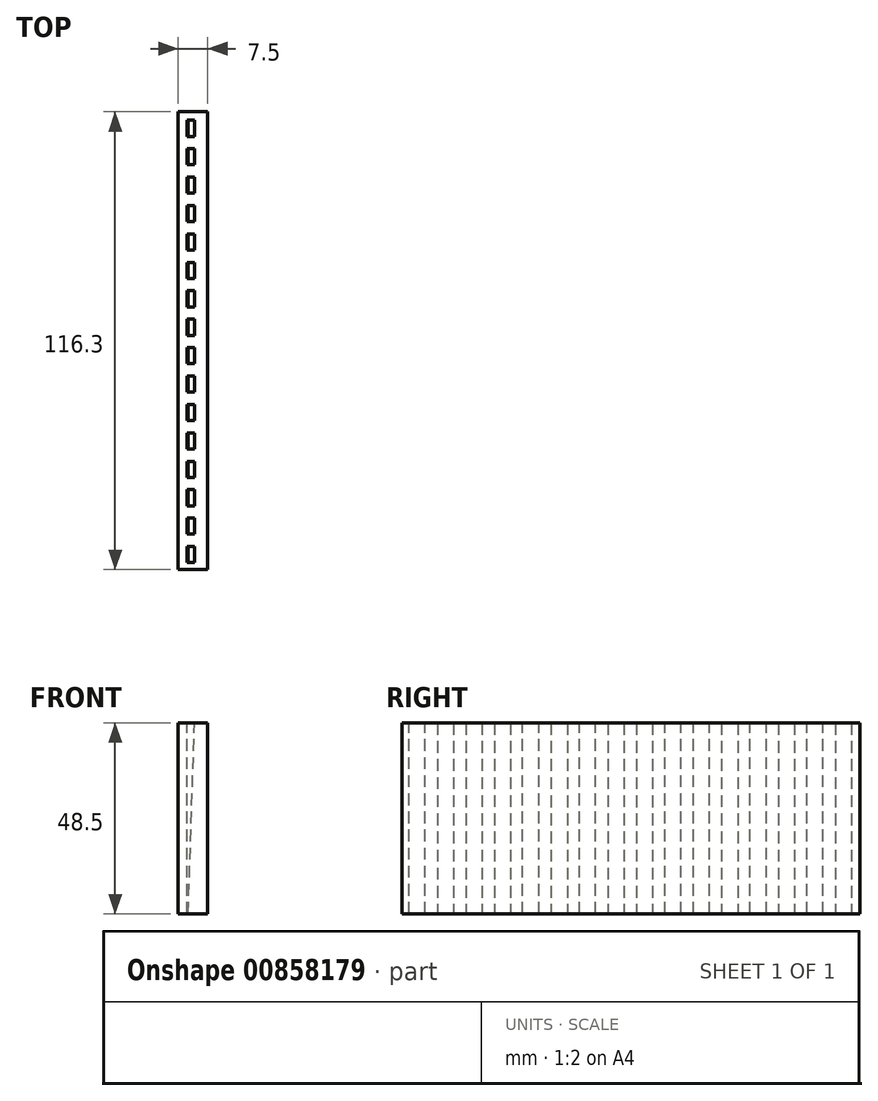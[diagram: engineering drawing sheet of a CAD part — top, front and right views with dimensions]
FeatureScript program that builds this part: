
annotation { "Feature Type Name" : "Feature", "Feature Type Description" : "" }
export const myFeature = defineFeature(function(context is Context, id is Id, definition is map)
    precondition{}
    {
        {
            var Q0;
            Q0=qCreatedBy(makeId("Right.planeOp"),FACE);
            var sketch = newSketch(context, id + "F0", { "sketchPlane" : qUnion([Q0])});
            skLineSegment(sketch, "E0.bottom", {"start": v(-70.88, 2.95) * mm, "end": v(80.42, 2.95) * mm});
            skLineSegment(sketch, "E0.top", {"start": v(-70.88, -45.55) * mm, "end": v(80.42, -45.55) * mm});
            skLineSegment(sketch, "E0.left", {"start": v(-70.88, 2.95) * mm, "end": v(-70.88, -45.55) * mm});
            skLineSegment(sketch, "E0.right", {"start": v(80.42, 2.95) * mm, "end": v(80.42, -45.55) * mm});
            skSolve(sketch);
        }
        {
            var Q0;
            Q0=makeQuery(id+"F0.imprint","IMPRINT",FACE,{"disambiguationData":[TD([[makeQuery(id+"F0.imprint","IMPRINT",EDGE,{"derivedFrom":sQuery(id+"F0.wireOp",EDGE,"E0.bottom")}),-1.0]])]});
            extrude(context, id + "F1", {"entities" : qUnion([Q0]), "depth" : 8 * mm, "offsetDistance" : 25 * mm});
        }
        {
            var Q0;
            Q0=makeQuery(id+"F1.opExtrude","SWEPT_FACE",FACE,{"disambiguationData":[OSD([sQuery(id+"F0.wireOp",EDGE,"E0.bottom")])]});
            var sketch = newSketch(context, id + "F2", { "sketchPlane" : qUnion([Q0])});
            skLineSegment(sketch, "E1.bottom", {"start": v(0.8, -69.15) * mm, "end": v(2.64, -69.15) * mm});
            skLineSegment(sketch, "E1.top", {"start": v(0.8, -65.05) * mm, "end": v(2.64, -65.05) * mm});
            skLineSegment(sketch, "E1.left", {"start": v(0.8, -69.15) * mm, "end": v(0.8, -65.05) * mm});
            skLineSegment(sketch, "E1.right", {"start": v(2.64, -69.15) * mm, "end": v(2.64, -65.05) * mm});
            skLineSegment(sketch, "E2.0.1.0", {"start": v(0.8, -61.93) * mm, "end": v(0.8, -57.83) * mm});
            skLineSegment(sketch, "E2.0.1.1", {"start": v(2.64, -61.93) * mm, "end": v(2.64, -57.83) * mm});
            skLineSegment(sketch, "E2.0.1.2", {"start": v(0.8, -61.93) * mm, "end": v(2.64, -61.93) * mm});
            skLineSegment(sketch, "E2.0.1.3", {"start": v(0.8, -57.83) * mm, "end": v(2.64, -57.83) * mm});
            skLineSegment(sketch, "E2.0.2.0", {"start": v(0.8, -54.7) * mm, "end": v(0.8, -50.6) * mm});
            skLineSegment(sketch, "E2.0.2.1", {"start": v(2.64, -54.7) * mm, "end": v(2.64, -50.6) * mm});
            skLineSegment(sketch, "E2.0.2.2", {"start": v(0.8, -54.7) * mm, "end": v(2.64, -54.7) * mm});
            skLineSegment(sketch, "E2.0.2.3", {"start": v(0.8, -50.6) * mm, "end": v(2.64, -50.6) * mm});
            skLineSegment(sketch, "E2.0.3.0", {"start": v(0.8, -47.49) * mm, "end": v(0.8, -43.39) * mm});
            skLineSegment(sketch, "E2.0.3.1", {"start": v(2.64, -47.49) * mm, "end": v(2.64, -43.39) * mm});
            skLineSegment(sketch, "E2.0.3.2", {"start": v(0.8, -47.49) * mm, "end": v(2.64, -47.49) * mm});
            skLineSegment(sketch, "E2.0.3.3", {"start": v(0.8, -43.39) * mm, "end": v(2.64, -43.39) * mm});
            skLineSegment(sketch, "E2.0.4.0", {"start": v(0.8, -40.27) * mm, "end": v(0.8, -36.17) * mm});
            skLineSegment(sketch, "E2.0.4.1", {"start": v(2.64, -40.27) * mm, "end": v(2.64, -36.17) * mm});
            skLineSegment(sketch, "E2.0.4.2", {"start": v(0.8, -40.27) * mm, "end": v(2.64, -40.27) * mm});
            skLineSegment(sketch, "E2.0.4.3", {"start": v(0.8, -36.17) * mm, "end": v(2.64, -36.17) * mm});
            skLineSegment(sketch, "E2.0.5.0", {"start": v(0.8, -33.05) * mm, "end": v(0.8, -28.95) * mm});
            skLineSegment(sketch, "E2.0.5.1", {"start": v(2.64, -33.05) * mm, "end": v(2.64, -28.95) * mm});
            skLineSegment(sketch, "E2.0.5.2", {"start": v(0.8, -33.05) * mm, "end": v(2.64, -33.05) * mm});
            skLineSegment(sketch, "E2.0.5.3", {"start": v(0.8, -28.95) * mm, "end": v(2.64, -28.95) * mm});
            skLineSegment(sketch, "E2.0.6.0", {"start": v(0.8, -25.83) * mm, "end": v(0.8, -21.73) * mm});
            skLineSegment(sketch, "E2.0.6.1", {"start": v(2.64, -25.83) * mm, "end": v(2.64, -21.73) * mm});
            skLineSegment(sketch, "E2.0.6.2", {"start": v(0.8, -25.83) * mm, "end": v(2.64, -25.83) * mm});
            skLineSegment(sketch, "E2.0.6.3", {"start": v(0.8, -21.73) * mm, "end": v(2.64, -21.73) * mm});
            skLineSegment(sketch, "E2.0.7.0", {"start": v(0.8, -18.6) * mm, "end": v(0.8, -14.5) * mm});
            skLineSegment(sketch, "E2.0.7.1", {"start": v(2.64, -18.6) * mm, "end": v(2.64, -14.5) * mm});
            skLineSegment(sketch, "E2.0.7.2", {"start": v(0.8, -18.6) * mm, "end": v(2.64, -18.6) * mm});
            skLineSegment(sketch, "E2.0.7.3", {"start": v(0.8, -14.5) * mm, "end": v(2.64, -14.5) * mm});
            skLineSegment(sketch, "E2.0.8.0", {"start": v(0.8, -11.39) * mm, "end": v(0.8, -7.29) * mm});
            skLineSegment(sketch, "E2.0.8.1", {"start": v(2.64, -11.39) * mm, "end": v(2.64, -7.29) * mm});
            skLineSegment(sketch, "E2.0.8.2", {"start": v(0.8, -11.39) * mm, "end": v(2.64, -11.39) * mm});
            skLineSegment(sketch, "E2.0.8.3", {"start": v(0.8, -7.29) * mm, "end": v(2.64, -7.29) * mm});
            skLineSegment(sketch, "E2.0.9.0", {"start": v(0.8, -4.17) * mm, "end": v(0.8, -0.07) * mm});
            skLineSegment(sketch, "E2.0.9.1", {"start": v(2.64, -4.17) * mm, "end": v(2.64, -0.07) * mm});
            skLineSegment(sketch, "E2.0.9.2", {"start": v(0.8, -4.17) * mm, "end": v(2.64, -4.17) * mm});
            skLineSegment(sketch, "E2.0.9.3", {"start": v(0.8, -0.07) * mm, "end": v(2.64, -0.07) * mm});
            skLineSegment(sketch, "E2.0.10.0", {"start": v(0.8, 3.05) * mm, "end": v(0.8, 7.15) * mm});
            skLineSegment(sketch, "E2.0.10.1", {"start": v(2.64, 3.05) * mm, "end": v(2.64, 7.15) * mm});
            skLineSegment(sketch, "E2.0.10.2", {"start": v(0.8, 3.05) * mm, "end": v(2.64, 3.05) * mm});
            skLineSegment(sketch, "E2.0.10.3", {"start": v(0.8, 7.15) * mm, "end": v(2.64, 7.15) * mm});
            skLineSegment(sketch, "E2.0.11.0", {"start": v(0.8, 10.27) * mm, "end": v(0.8, 14.37) * mm});
            skLineSegment(sketch, "E2.0.11.1", {"start": v(2.64, 10.27) * mm, "end": v(2.64, 14.37) * mm});
            skLineSegment(sketch, "E2.0.11.2", {"start": v(0.8, 10.27) * mm, "end": v(2.64, 10.27) * mm});
            skLineSegment(sketch, "E2.0.11.3", {"start": v(0.8, 14.37) * mm, "end": v(2.64, 14.37) * mm});
            skLineSegment(sketch, "E2.0.12.0", {"start": v(0.8, 17.5) * mm, "end": v(0.8, 21.6) * mm});
            skLineSegment(sketch, "E2.0.12.1", {"start": v(2.64, 17.5) * mm, "end": v(2.64, 21.6) * mm});
            skLineSegment(sketch, "E2.0.12.2", {"start": v(0.8, 17.5) * mm, "end": v(2.64, 17.5) * mm});
            skLineSegment(sketch, "E2.0.12.3", {"start": v(0.8, 21.6) * mm, "end": v(2.64, 21.6) * mm});
            skLineSegment(sketch, "E2.0.13.0", {"start": v(0.8, 24.71) * mm, "end": v(0.8, 28.81) * mm});
            skLineSegment(sketch, "E2.0.13.1", {"start": v(2.64, 24.71) * mm, "end": v(2.64, 28.81) * mm});
            skLineSegment(sketch, "E2.0.13.2", {"start": v(0.8, 24.71) * mm, "end": v(2.64, 24.71) * mm});
            skLineSegment(sketch, "E2.0.13.3", {"start": v(0.8, 28.81) * mm, "end": v(2.64, 28.81) * mm});
            skLineSegment(sketch, "E2.0.14.0", {"start": v(0.8, 31.93) * mm, "end": v(0.8, 36.03) * mm});
            skLineSegment(sketch, "E2.0.14.1", {"start": v(2.64, 31.93) * mm, "end": v(2.64, 36.03) * mm});
            skLineSegment(sketch, "E2.0.14.2", {"start": v(0.8, 31.93) * mm, "end": v(2.64, 31.93) * mm});
            skLineSegment(sketch, "E2.0.14.3", {"start": v(0.8, 36.03) * mm, "end": v(2.64, 36.03) * mm});
            skLineSegment(sketch, "E2.0.15.0", {"start": v(0.8, 39.15) * mm, "end": v(0.8, 43.25) * mm});
            skLineSegment(sketch, "E2.0.15.1", {"start": v(2.64, 39.15) * mm, "end": v(2.64, 43.25) * mm});
            skLineSegment(sketch, "E2.0.15.2", {"start": v(0.8, 39.15) * mm, "end": v(2.64, 39.15) * mm});
            skLineSegment(sketch, "E2.0.15.3", {"start": v(0.8, 43.25) * mm, "end": v(2.64, 43.25) * mm});
            skLineSegment(sketch, "E2.direction1", {"start": v(0.8, -69.15) * mm, "end": v(0.8, -69.15) * mm});
            skLineSegment(sketch, "E2.direction2", {"start": v(0.8, -69.15) * mm, "end": v(0.8, -61.93) * mm, "construction": true});
            skSolve(sketch);
        }
        {
            var Q0;
            Q0=makeQuery(id+"F1.opExtrude","SWEPT_FACE",FACE,{"disambiguationData":[OSD([sQuery(id+"F0.wireOp",EDGE,"E0.top")])]});
            var sketch = newSketch(context, id + "F3", { "sketchPlane" : qUnion([Q0])});
            skLineSegment(sketch, "E3.bottom", {"start": v(0.78, 69.14) * mm, "end": v(1.03, 69.14) * mm});
            skLineSegment(sketch, "E3.top", {"start": v(0.78, 65.04) * mm, "end": v(1.03, 65.04) * mm});
            skLineSegment(sketch, "E3.left", {"start": v(0.78, 69.14) * mm, "end": v(0.78, 65.04) * mm});
            skLineSegment(sketch, "E3.right", {"start": v(1.03, 69.14) * mm, "end": v(1.03, 65.04) * mm});
            skLineSegment(sketch, "E4.0.1.0", {"start": v(1.03, 61.92) * mm, "end": v(1.03, 57.82) * mm});
            skLineSegment(sketch, "E4.0.1.1", {"start": v(0.78, 61.92) * mm, "end": v(0.78, 57.82) * mm});
            skLineSegment(sketch, "E4.0.1.2", {"start": v(0.78, 61.92) * mm, "end": v(1.03, 61.92) * mm});
            skLineSegment(sketch, "E4.0.1.3", {"start": v(0.78, 57.82) * mm, "end": v(1.03, 57.82) * mm});
            skLineSegment(sketch, "E4.0.2.0", {"start": v(1.03, 54.7) * mm, "end": v(1.03, 50.6) * mm});
            skLineSegment(sketch, "E4.0.2.1", {"start": v(0.78, 54.7) * mm, "end": v(0.78, 50.6) * mm});
            skLineSegment(sketch, "E4.0.2.2", {"start": v(0.78, 54.7) * mm, "end": v(1.03, 54.7) * mm});
            skLineSegment(sketch, "E4.0.2.3", {"start": v(0.78, 50.6) * mm, "end": v(1.03, 50.6) * mm});
            skLineSegment(sketch, "E4.0.3.0", {"start": v(1.03, 47.48) * mm, "end": v(1.03, 43.38) * mm});
            skLineSegment(sketch, "E4.0.3.1", {"start": v(0.78, 47.48) * mm, "end": v(0.78, 43.38) * mm});
            skLineSegment(sketch, "E4.0.3.2", {"start": v(0.78, 47.48) * mm, "end": v(1.03, 47.48) * mm});
            skLineSegment(sketch, "E4.0.3.3", {"start": v(0.78, 43.38) * mm, "end": v(1.03, 43.38) * mm});
            skLineSegment(sketch, "E4.0.4.0", {"start": v(1.03, 40.26) * mm, "end": v(1.03, 36.16) * mm});
            skLineSegment(sketch, "E4.0.4.1", {"start": v(0.78, 40.26) * mm, "end": v(0.78, 36.16) * mm});
            skLineSegment(sketch, "E4.0.4.2", {"start": v(0.78, 40.26) * mm, "end": v(1.03, 40.26) * mm});
            skLineSegment(sketch, "E4.0.4.3", {"start": v(0.78, 36.16) * mm, "end": v(1.03, 36.16) * mm});
            skLineSegment(sketch, "E4.0.5.0", {"start": v(1.03, 33.04) * mm, "end": v(1.03, 28.94) * mm});
            skLineSegment(sketch, "E4.0.5.1", {"start": v(0.78, 33.04) * mm, "end": v(0.78, 28.94) * mm});
            skLineSegment(sketch, "E4.0.5.2", {"start": v(0.78, 33.04) * mm, "end": v(1.03, 33.04) * mm});
            skLineSegment(sketch, "E4.0.5.3", {"start": v(0.78, 28.94) * mm, "end": v(1.03, 28.94) * mm});
            skLineSegment(sketch, "E4.0.6.0", {"start": v(1.03, 25.82) * mm, "end": v(1.03, 21.72) * mm});
            skLineSegment(sketch, "E4.0.6.1", {"start": v(0.78, 25.82) * mm, "end": v(0.78, 21.72) * mm});
            skLineSegment(sketch, "E4.0.6.2", {"start": v(0.78, 25.82) * mm, "end": v(1.03, 25.82) * mm});
            skLineSegment(sketch, "E4.0.6.3", {"start": v(0.78, 21.72) * mm, "end": v(1.03, 21.72) * mm});
            skLineSegment(sketch, "E4.0.7.0", {"start": v(1.03, 18.6) * mm, "end": v(1.03, 14.5) * mm});
            skLineSegment(sketch, "E4.0.7.1", {"start": v(0.78, 18.6) * mm, "end": v(0.78, 14.5) * mm});
            skLineSegment(sketch, "E4.0.7.2", {"start": v(0.78, 18.6) * mm, "end": v(1.03, 18.6) * mm});
            skLineSegment(sketch, "E4.0.7.3", {"start": v(0.78, 14.5) * mm, "end": v(1.03, 14.5) * mm});
            skLineSegment(sketch, "E4.0.8.0", {"start": v(1.03, 11.38) * mm, "end": v(1.03, 7.28) * mm});
            skLineSegment(sketch, "E4.0.8.1", {"start": v(0.78, 11.38) * mm, "end": v(0.78, 7.28) * mm});
            skLineSegment(sketch, "E4.0.8.2", {"start": v(0.78, 11.38) * mm, "end": v(1.03, 11.38) * mm});
            skLineSegment(sketch, "E4.0.8.3", {"start": v(0.78, 7.28) * mm, "end": v(1.03, 7.28) * mm});
            skLineSegment(sketch, "E4.0.9.0", {"start": v(1.03, 4.16) * mm, "end": v(1.03, 0.06) * mm});
            skLineSegment(sketch, "E4.0.9.1", {"start": v(0.78, 4.16) * mm, "end": v(0.78, 0.06) * mm});
            skLineSegment(sketch, "E4.0.9.2", {"start": v(0.78, 4.16) * mm, "end": v(1.03, 4.16) * mm});
            skLineSegment(sketch, "E4.0.9.3", {"start": v(0.78, 0.06) * mm, "end": v(1.03, 0.06) * mm});
            skLineSegment(sketch, "E4.0.10.0", {"start": v(1.03, -3.06) * mm, "end": v(1.03, -7.16) * mm});
            skLineSegment(sketch, "E4.0.10.1", {"start": v(0.78, -3.06) * mm, "end": v(0.78, -7.16) * mm});
            skLineSegment(sketch, "E4.0.10.2", {"start": v(0.78, -3.06) * mm, "end": v(1.03, -3.06) * mm});
            skLineSegment(sketch, "E4.0.10.3", {"start": v(0.78, -7.16) * mm, "end": v(1.03, -7.16) * mm});
            skLineSegment(sketch, "E4.0.11.0", {"start": v(1.03, -10.28) * mm, "end": v(1.03, -14.38) * mm});
            skLineSegment(sketch, "E4.0.11.1", {"start": v(0.78, -10.28) * mm, "end": v(0.78, -14.38) * mm});
            skLineSegment(sketch, "E4.0.11.2", {"start": v(0.78, -10.28) * mm, "end": v(1.03, -10.28) * mm});
            skLineSegment(sketch, "E4.0.11.3", {"start": v(0.78, -14.38) * mm, "end": v(1.03, -14.38) * mm});
            skLineSegment(sketch, "E4.0.12.0", {"start": v(1.03, -17.5) * mm, "end": v(1.03, -21.6) * mm});
            skLineSegment(sketch, "E4.0.12.1", {"start": v(0.78, -17.5) * mm, "end": v(0.78, -21.6) * mm});
            skLineSegment(sketch, "E4.0.12.2", {"start": v(0.78, -17.5) * mm, "end": v(1.03, -17.5) * mm});
            skLineSegment(sketch, "E4.0.12.3", {"start": v(0.78, -21.6) * mm, "end": v(1.03, -21.6) * mm});
            skLineSegment(sketch, "E4.0.13.0", {"start": v(1.03, -24.72) * mm, "end": v(1.03, -28.82) * mm});
            skLineSegment(sketch, "E4.0.13.1", {"start": v(0.78, -24.72) * mm, "end": v(0.78, -28.82) * mm});
            skLineSegment(sketch, "E4.0.13.2", {"start": v(0.78, -24.72) * mm, "end": v(1.03, -24.72) * mm});
            skLineSegment(sketch, "E4.0.13.3", {"start": v(0.78, -28.82) * mm, "end": v(1.03, -28.82) * mm});
            skLineSegment(sketch, "E4.0.14.0", {"start": v(1.03, -31.94) * mm, "end": v(1.03, -36.04) * mm});
            skLineSegment(sketch, "E4.0.14.1", {"start": v(0.78, -31.94) * mm, "end": v(0.78, -36.04) * mm});
            skLineSegment(sketch, "E4.0.14.2", {"start": v(0.78, -31.94) * mm, "end": v(1.03, -31.94) * mm});
            skLineSegment(sketch, "E4.0.14.3", {"start": v(0.78, -36.04) * mm, "end": v(1.03, -36.04) * mm});
            skLineSegment(sketch, "E4.0.15.0", {"start": v(1.03, -39.16) * mm, "end": v(1.03, -43.26) * mm});
            skLineSegment(sketch, "E4.0.15.1", {"start": v(0.78, -39.16) * mm, "end": v(0.78, -43.26) * mm});
            skLineSegment(sketch, "E4.0.15.2", {"start": v(0.78, -39.16) * mm, "end": v(1.03, -39.16) * mm});
            skLineSegment(sketch, "E4.0.15.3", {"start": v(0.78, -43.26) * mm, "end": v(1.03, -43.26) * mm});
            skLineSegment(sketch, "E4.direction1", {"start": v(0.78, 65.04) * mm, "end": v(0.78, 65.04) * mm});
            skLineSegment(sketch, "E4.direction2", {"start": v(0.78, 65.04) * mm, "end": v(0.78, 57.82) * mm, "construction": true});
            skSolve(sketch);
        }
        {
            var Q1;
            Q1=makeQuery(id+"F2.imprint","IMPRINT",FACE,{"disambiguationData":[TD([[makeQuery(id+"F2.imprint","IMPRINT",EDGE,{"derivedFrom":sQuery(id+"F2.wireOp",EDGE,"E1.bottom")}),1.0]])]});
            var Q2;
            Q2=makeQuery(id+"F3.imprint","IMPRINT",FACE,{"disambiguationData":[TD([[makeQuery(id+"F3.imprint","IMPRINT",EDGE,{"derivedFrom":sQuery(id+"F3.wireOp",EDGE,"E3.bottom")}),-1.0]])]});
            loft(context, id + "F4", {"operationType" : NewBodyOperationType.ADD, "sheetProfilesArray" : [{ "sheetProfileEntities" : qUnion([Q1]) }, { "sheetProfileEntities" : qUnion([Q2]) }]});
        }
        {
            var Q1;
            Q1=makeQuery(id+"F3.imprint","IMPRINT",FACE,{"disambiguationData":[TD([[makeQuery(id+"F3.imprint","IMPRINT",EDGE,{"derivedFrom":sQuery(id+"F3.wireOp",EDGE,"E3.bottom")}),-1.0]])]});
            var Q2;
            Q2=makeQuery(id+"F2.imprint","IMPRINT",FACE,{"disambiguationData":[TD([[makeQuery(id+"F2.imprint","IMPRINT",EDGE,{"derivedFrom":sQuery(id+"F2.wireOp",EDGE,"E1.bottom")}),1.0]])]});
            var Q3;
            Q3=sQuery(id+"F2.wireOp",VERTEX,"E1.top.end");
            var Q4;
            Q4=sQuery(id+"F3.wireOp",VERTEX,"E3.top.end");
            var Q5;
            Q5=sQuery(id+"F3.wireOp",VERTEX,"E3.top.start");
            var Q6;
            Q6=sQuery(id+"F2.wireOp",VERTEX,"E1.top.start");
            var Q7;
            Q7=sQuery(id+"F3.wireOp",VERTEX,"E3.bottom.start");
            var Q8;
            Q8=sQuery(id+"F2.wireOp",VERTEX,"E1.bottom.start");
            var Q9;
            Q9=sQuery(id+"F2.wireOp",VERTEX,"E1.bottom.end");
            var Q10;
            Q10=sQuery(id+"F3.wireOp",VERTEX,"E3.bottom.end");
            loft(context, id + "F5", {"operationType" : NewBodyOperationType.REMOVE, "sheetProfilesArray" : [{ "sheetProfileEntities" : qUnion([Q1]) }, { "sheetProfileEntities" : qUnion([Q2]) }], "connections" : [{ "connectionEntities" : qUnion([Q3, Q4, Q5, Q6, Q7, Q8, Q9, Q10]), "connectionEdgeQueries" : qUnion([]), "connectionEdgeParameters" : [] }]});
        }
        {
            var Q1;
            Q1=makeQuery(id+"F2.imprint","IMPRINT",FACE,{"disambiguationData":[TD([[makeQuery(id+"F2.imprint","IMPRINT",EDGE,{"derivedFrom":sQuery(id+"F2.wireOp",EDGE,"E2.0.1.0")}),-1.0]])]});
            var Q2;
            Q2=makeQuery(id+"F3.imprint","IMPRINT",FACE,{"disambiguationData":[TD([[makeQuery(id+"F3.imprint","IMPRINT",EDGE,{"derivedFrom":sQuery(id+"F3.wireOp",EDGE,"E4.0.1.0")}),-1.0]])]});
            loft(context, id + "F6", {"operationType" : NewBodyOperationType.REMOVE, "sheetProfilesArray" : [{ "sheetProfileEntities" : qUnion([Q1]) }, { "sheetProfileEntities" : qUnion([Q2]) }]});
        }
        {
            var Q1;
            Q1=makeQuery(id+"F2.imprint","IMPRINT",FACE,{"disambiguationData":[TD([[makeQuery(id+"F2.imprint","IMPRINT",EDGE,{"derivedFrom":sQuery(id+"F2.wireOp",EDGE,"E2.0.2.0")}),-1.0]])]});
            var Q2;
            Q2=makeQuery(id+"F3.imprint","IMPRINT",FACE,{"disambiguationData":[TD([[makeQuery(id+"F3.imprint","IMPRINT",EDGE,{"derivedFrom":sQuery(id+"F3.wireOp",EDGE,"E4.0.2.0")}),-1.0]])]});
            loft(context, id + "F7", {"operationType" : NewBodyOperationType.REMOVE, "sheetProfilesArray" : [{ "sheetProfileEntities" : qUnion([Q1]) }, { "sheetProfileEntities" : qUnion([Q2]) }]});
        }
        {
            var Q1;
            Q1=makeQuery(id+"F2.imprint","IMPRINT",FACE,{"disambiguationData":[TD([[makeQuery(id+"F2.imprint","IMPRINT",EDGE,{"derivedFrom":sQuery(id+"F2.wireOp",EDGE,"E2.0.3.0")}),-1.0]])]});
            var Q2;
            Q2=makeQuery(id+"F3.imprint","IMPRINT",FACE,{"disambiguationData":[TD([[makeQuery(id+"F3.imprint","IMPRINT",EDGE,{"derivedFrom":sQuery(id+"F3.wireOp",EDGE,"E4.0.3.0")}),-1.0]])]});
            loft(context, id + "F8", {"operationType" : NewBodyOperationType.REMOVE, "sheetProfilesArray" : [{ "sheetProfileEntities" : qUnion([Q1]) }, { "sheetProfileEntities" : qUnion([Q2]) }]});
        }
        {
            var Q1;
            Q1=makeQuery(id+"F3.imprint","IMPRINT",FACE,{"disambiguationData":[TD([[makeQuery(id+"F3.imprint","IMPRINT",EDGE,{"derivedFrom":sQuery(id+"F3.wireOp",EDGE,"E4.0.4.0")}),-1.0]])]});
            var Q2;
            Q2=makeQuery(id+"F2.imprint","IMPRINT",FACE,{"disambiguationData":[TD([[makeQuery(id+"F2.imprint","IMPRINT",EDGE,{"derivedFrom":sQuery(id+"F2.wireOp",EDGE,"E2.0.4.0")}),-1.0]])]});
            loft(context, id + "F9", {"operationType" : NewBodyOperationType.REMOVE, "sheetProfilesArray" : [{ "sheetProfileEntities" : qUnion([Q1]) }, { "sheetProfileEntities" : qUnion([Q2]) }]});
        }
        {
            var Q1;
            Q1=makeQuery(id+"F2.imprint","IMPRINT",FACE,{"disambiguationData":[TD([[makeQuery(id+"F2.imprint","IMPRINT",EDGE,{"derivedFrom":sQuery(id+"F2.wireOp",EDGE,"E2.0.5.0")}),-1.0]])]});
            var Q2;
            Q2=makeQuery(id+"F3.imprint","IMPRINT",FACE,{"disambiguationData":[TD([[makeQuery(id+"F3.imprint","IMPRINT",EDGE,{"derivedFrom":sQuery(id+"F3.wireOp",EDGE,"E4.0.5.0")}),-1.0]])]});
            loft(context, id + "F10", {"operationType" : NewBodyOperationType.REMOVE, "sheetProfilesArray" : [{ "sheetProfileEntities" : qUnion([Q1]) }, { "sheetProfileEntities" : qUnion([Q2]) }]});
        }
        {
            var Q1;
            Q1=makeQuery(id+"F3.imprint","IMPRINT",FACE,{"disambiguationData":[TD([[makeQuery(id+"F3.imprint","IMPRINT",EDGE,{"derivedFrom":sQuery(id+"F3.wireOp",EDGE,"E4.0.6.0")}),-1.0]])]});
            var Q2;
            Q2=makeQuery(id+"F2.imprint","IMPRINT",FACE,{"disambiguationData":[TD([[makeQuery(id+"F2.imprint","IMPRINT",EDGE,{"derivedFrom":sQuery(id+"F2.wireOp",EDGE,"E2.0.6.0")}),-1.0]])]});
            loft(context, id + "F11", {"operationType" : NewBodyOperationType.REMOVE, "sheetProfilesArray" : [{ "sheetProfileEntities" : qUnion([Q1]) }, { "sheetProfileEntities" : qUnion([Q2]) }]});
        }
        {
            var Q1;
            Q1=makeQuery(id+"F2.imprint","IMPRINT",FACE,{"disambiguationData":[TD([[makeQuery(id+"F2.imprint","IMPRINT",EDGE,{"derivedFrom":sQuery(id+"F2.wireOp",EDGE,"E2.0.7.0")}),-1.0]])]});
            var Q2;
            Q2=makeQuery(id+"F3.imprint","IMPRINT",FACE,{"disambiguationData":[TD([[makeQuery(id+"F3.imprint","IMPRINT",EDGE,{"derivedFrom":sQuery(id+"F3.wireOp",EDGE,"E4.0.7.0")}),-1.0]])]});
            loft(context, id + "F12", {"operationType" : NewBodyOperationType.ADD, "sheetProfilesArray" : [{ "sheetProfileEntities" : qUnion([Q1]) }, { "sheetProfileEntities" : qUnion([Q2]) }]});
        }
        {
            var Q1;
            Q1=makeQuery(id+"F2.imprint","IMPRINT",FACE,{"disambiguationData":[TD([[makeQuery(id+"F2.imprint","IMPRINT",EDGE,{"derivedFrom":sQuery(id+"F2.wireOp",EDGE,"E2.0.7.0")}),-1.0]])]});
            var Q2;
            Q2=makeQuery(id+"F3.imprint","IMPRINT",FACE,{"disambiguationData":[TD([[makeQuery(id+"F3.imprint","IMPRINT",EDGE,{"derivedFrom":sQuery(id+"F3.wireOp",EDGE,"E4.0.7.0")}),-1.0]])]});
            loft(context, id + "F13", {"operationType" : NewBodyOperationType.REMOVE, "sheetProfilesArray" : [{ "sheetProfileEntities" : qUnion([Q1]) }, { "sheetProfileEntities" : qUnion([Q2]) }]});
        }
        {
            var Q1;
            Q1=makeQuery(id+"F2.imprint","IMPRINT",FACE,{"disambiguationData":[TD([[makeQuery(id+"F2.imprint","IMPRINT",EDGE,{"derivedFrom":sQuery(id+"F2.wireOp",EDGE,"E2.0.8.0")}),-1.0]])]});
            var Q2;
            Q2=makeQuery(id+"F3.imprint","IMPRINT",FACE,{"disambiguationData":[TD([[makeQuery(id+"F3.imprint","IMPRINT",EDGE,{"derivedFrom":sQuery(id+"F3.wireOp",EDGE,"E4.0.8.0")}),-1.0]])]});
            loft(context, id + "F14", {"operationType" : NewBodyOperationType.REMOVE, "sheetProfilesArray" : [{ "sheetProfileEntities" : qUnion([Q1]) }, { "sheetProfileEntities" : qUnion([Q2]) }]});
        }
        {
            var Q1;
            Q1=makeQuery(id+"F3.imprint","IMPRINT",FACE,{"disambiguationData":[TD([[makeQuery(id+"F3.imprint","IMPRINT",EDGE,{"derivedFrom":sQuery(id+"F3.wireOp",EDGE,"E4.0.9.0")}),-1.0]])]});
            var Q2;
            Q2=makeQuery(id+"F2.imprint","IMPRINT",FACE,{"disambiguationData":[TD([[makeQuery(id+"F2.imprint","IMPRINT",EDGE,{"derivedFrom":sQuery(id+"F2.wireOp",EDGE,"E2.0.9.0")}),-1.0]])]});
            loft(context, id + "F15", {"operationType" : NewBodyOperationType.REMOVE, "sheetProfilesArray" : [{ "sheetProfileEntities" : qUnion([Q1]) }, { "sheetProfileEntities" : qUnion([Q2]) }]});
        }
        {
            var Q1;
            Q1=makeQuery(id+"F3.imprint","IMPRINT",FACE,{"disambiguationData":[TD([[makeQuery(id+"F3.imprint","IMPRINT",EDGE,{"derivedFrom":sQuery(id+"F3.wireOp",EDGE,"E4.0.10.0")}),-1.0]])]});
            var Q2;
            Q2=makeQuery(id+"F2.imprint","IMPRINT",FACE,{"disambiguationData":[TD([[makeQuery(id+"F2.imprint","IMPRINT",EDGE,{"derivedFrom":sQuery(id+"F2.wireOp",EDGE,"E2.0.10.0")}),-1.0]])]});
            loft(context, id + "F16", {"operationType" : NewBodyOperationType.REMOVE, "sheetProfilesArray" : [{ "sheetProfileEntities" : qUnion([Q1]) }, { "sheetProfileEntities" : qUnion([Q2]) }]});
        }
        {
            var Q1;
            Q1=makeQuery(id+"F2.imprint","IMPRINT",FACE,{"disambiguationData":[TD([[makeQuery(id+"F2.imprint","IMPRINT",EDGE,{"derivedFrom":sQuery(id+"F2.wireOp",EDGE,"E2.0.11.0")}),-1.0]])]});
            var Q2;
            Q2=makeQuery(id+"F3.imprint","IMPRINT",FACE,{"disambiguationData":[TD([[makeQuery(id+"F3.imprint","IMPRINT",EDGE,{"derivedFrom":sQuery(id+"F3.wireOp",EDGE,"E4.0.11.0")}),-1.0]])]});
            loft(context, id + "F17", {"operationType" : NewBodyOperationType.REMOVE, "sheetProfilesArray" : [{ "sheetProfileEntities" : qUnion([Q1]) }, { "sheetProfileEntities" : qUnion([Q2]) }]});
        }
        {
            var Q1;
            Q1=makeQuery(id+"F3.imprint","IMPRINT",FACE,{"disambiguationData":[TD([[makeQuery(id+"F3.imprint","IMPRINT",EDGE,{"derivedFrom":sQuery(id+"F3.wireOp",EDGE,"E4.0.12.0")}),-1.0]])]});
            var Q2;
            Q2=makeQuery(id+"F2.imprint","IMPRINT",FACE,{"disambiguationData":[TD([[makeQuery(id+"F2.imprint","IMPRINT",EDGE,{"derivedFrom":sQuery(id+"F2.wireOp",EDGE,"E2.0.12.0")}),-1.0]])]});
            loft(context, id + "F18", {"operationType" : NewBodyOperationType.REMOVE, "sheetProfilesArray" : [{ "sheetProfileEntities" : qUnion([Q1]) }, { "sheetProfileEntities" : qUnion([Q2]) }]});
        }
        {
            var Q1;
            Q1=makeQuery(id+"F2.imprint","IMPRINT",FACE,{"disambiguationData":[TD([[makeQuery(id+"F2.imprint","IMPRINT",EDGE,{"derivedFrom":sQuery(id+"F2.wireOp",EDGE,"E2.0.13.0")}),-1.0]])]});
            var Q2;
            Q2=makeQuery(id+"F3.imprint","IMPRINT",FACE,{"disambiguationData":[TD([[makeQuery(id+"F3.imprint","IMPRINT",EDGE,{"derivedFrom":sQuery(id+"F3.wireOp",EDGE,"E4.0.13.0")}),-1.0]])]});
            loft(context, id + "F19", {"operationType" : NewBodyOperationType.REMOVE, "sheetProfilesArray" : [{ "sheetProfileEntities" : qUnion([Q1]) }, { "sheetProfileEntities" : qUnion([Q2]) }]});
        }
        {
            var Q1;
            Q1=makeQuery(id+"F3.imprint","IMPRINT",FACE,{"disambiguationData":[TD([[makeQuery(id+"F3.imprint","IMPRINT",EDGE,{"derivedFrom":sQuery(id+"F3.wireOp",EDGE,"E4.0.14.0")}),-1.0]])]});
            var Q2;
            Q2=makeQuery(id+"F2.imprint","IMPRINT",FACE,{"disambiguationData":[TD([[makeQuery(id+"F2.imprint","IMPRINT",EDGE,{"derivedFrom":sQuery(id+"F2.wireOp",EDGE,"E2.0.14.0")}),-1.0]])]});
            loft(context, id + "F20", {"operationType" : NewBodyOperationType.REMOVE, "sheetProfilesArray" : [{ "sheetProfileEntities" : qUnion([Q1]) }, { "sheetProfileEntities" : qUnion([Q2]) }]});
        }
        {
            var Q1;
            Q1=makeQuery(id+"F2.imprint","IMPRINT",FACE,{"disambiguationData":[TD([[makeQuery(id+"F2.imprint","IMPRINT",EDGE,{"derivedFrom":sQuery(id+"F2.wireOp",EDGE,"E2.0.15.0")}),-1.0]])]});
            var Q2;
            Q2=makeQuery(id+"F3.imprint","IMPRINT",FACE,{"disambiguationData":[TD([[makeQuery(id+"F3.imprint","IMPRINT",EDGE,{"derivedFrom":sQuery(id+"F3.wireOp",EDGE,"E4.0.15.0")}),-1.0]])]});
            loft(context, id + "F21", {"operationType" : NewBodyOperationType.REMOVE, "sheetProfilesArray" : [{ "sheetProfileEntities" : qUnion([Q1]) }, { "sheetProfileEntities" : qUnion([Q2]) }]});
        }
        {
            var Q0;
            Q0=makeQuery(id+"F1.opExtrude","CAP_FACE",FACE,{"disambiguationData":[OSD([sQuery(id+"F0.wireOp",EDGE,"E0.bottom"),sQuery(id+"F0.wireOp",EDGE,"E0.top"),sQuery(id+"F0.wireOp",EDGE,"E0.left"),sQuery(id+"F0.wireOp",EDGE,"E0.right")])],"isStart":true});
            extrude(context, id + "F22", {"entities" : qUnion([Q0]), "operationType" : NewBodyOperationType.ADD, "depth" : 1.5 * mm, "offsetDistance" : 25 * mm});
        }
        {
            var Q0;
            Q0=makeQuery(id+"F1.opExtrude","CAP_FACE",FACE,{"disambiguationData":[OSD([sQuery(id+"F0.wireOp",EDGE,"E0.bottom"),sQuery(id+"F0.wireOp",EDGE,"E0.top"),sQuery(id+"F0.wireOp",EDGE,"E0.left"),sQuery(id+"F0.wireOp",EDGE,"E0.right")])],"isStart":false});
            extrude(context, id + "F23", {"entities" : qUnion([Q0]), "operationType" : NewBodyOperationType.REMOVE, "oppositeDirection" : true, "depth" : 2 * mm, "offsetDistance" : 25 * mm});
        }
        {
            var Q0;
            {var subQ0=sQuery(id+"F0.wireOp",EDGE,"E0.right");Q0=makeQuery(id+"F22.boolean.opBoolean","MERGE",FACE,{"derivedFrom":[makeQuery(id+"F1.opExtrude","SWEPT_FACE",FACE,{"disambiguationData":[OSD([subQ0])]}),makeQuery(id+"F22.opExtrude","SWEPT_FACE",FACE,{"disambiguationData":[OSD([subQ0])]})]});}
            extrude(context, id + "F24", {"entities" : qUnion([Q0]), "operationType" : NewBodyOperationType.REMOVE, "oppositeDirection" : true, "depth" : 35 * mm, "offsetDistance" : 25 * mm});
        }
    });
